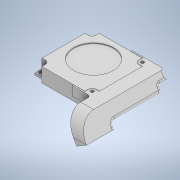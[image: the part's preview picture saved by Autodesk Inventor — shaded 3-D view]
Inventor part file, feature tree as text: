
AUTODESK INVENTOR PART (.ipt)
format: ipt  version: 2020.2 (Build 242310000, 310)  size: 607,744 bytes
history: native  units: mm
features: other x5, plane x2, mirror x1
ambient origin geometry x8: Origin, YZ Plane, XZ Plane, XY Plane, X Axis, Y Axis, Z Axis, Center Point
bodies: Solid3 (feature_tree), Solid1 (feature_tree), Solid2 (feature_tree)
feature tree (8):
  other  "4010B_fan.ipt"
  mirror  "Mirror1"
  other  "Solid1::4010B_fan.ipt"
  other  "Solid3::4010B_fan.ipt"
  other  "TaggingFeature1"
  plane  "Work Plane1"
  plane  "Work Plane2"
  other  "Pattern of Solid2:1"
